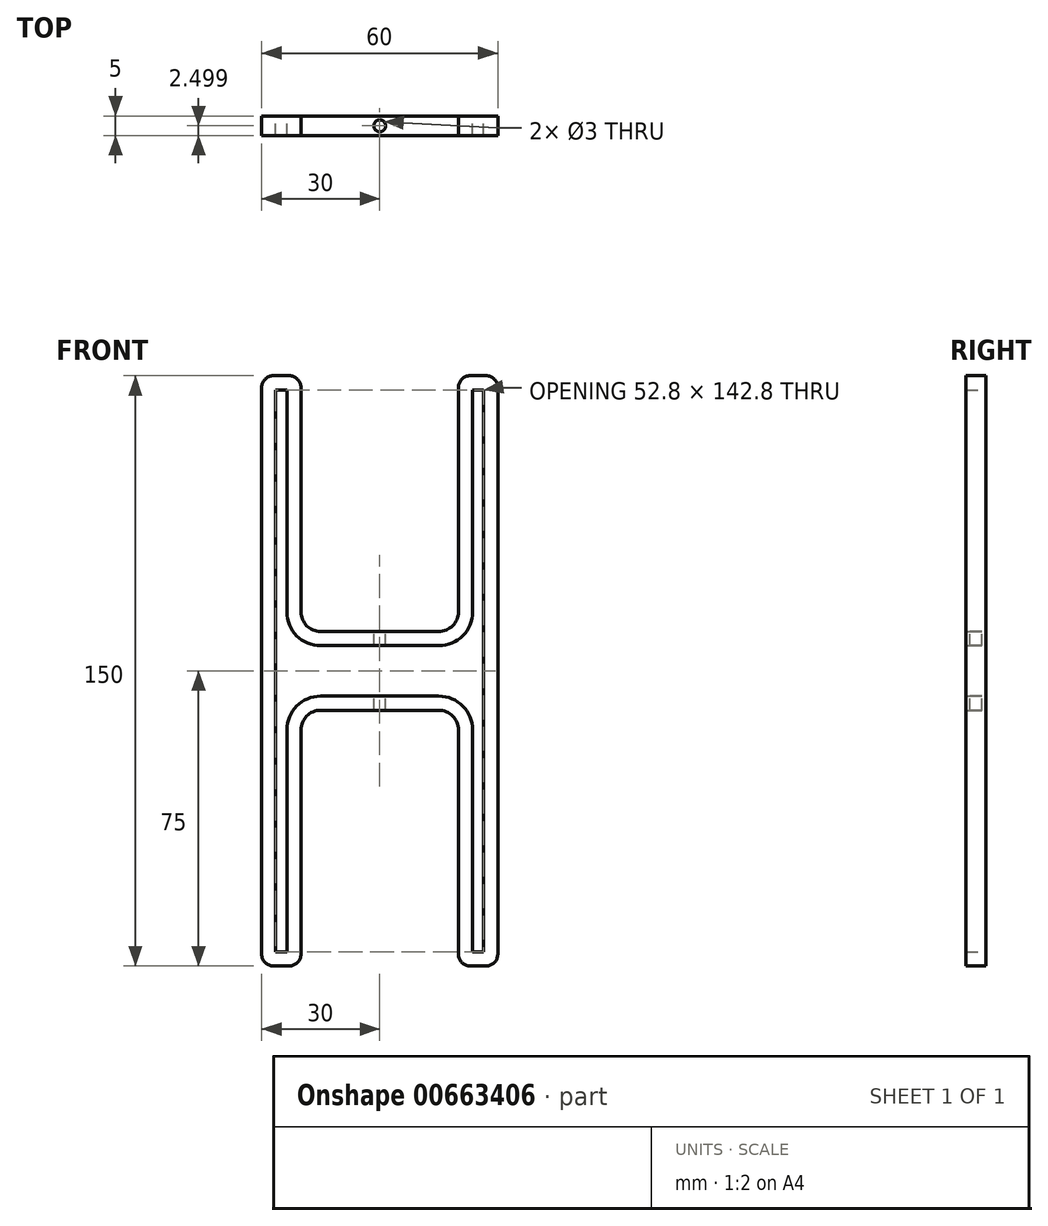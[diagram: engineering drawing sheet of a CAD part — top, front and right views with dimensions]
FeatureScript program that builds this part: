
annotation { "Feature Type Name" : "Feature", "Feature Type Description" : "" }
export const myFeature = defineFeature(function(context is Context, id is Id, definition is map)
    precondition{}
    {
        {
            var Q0;
            Q0=qCreatedBy(makeId("Front.planeOp"),FACE);
            var sketch = newSketch(context, id + "F0", { "sketchPlane" : qUnion([Q0])});
            skLineSegment(sketch, "E0.bottom", {"start": v(-27, 75) * mm, "end": v(-23, 75) * mm});
            skLineSegment(sketch, "E0.top", {"start": v(-27, -75) * mm, "end": v(-23, -75) * mm});
            skLineSegment(sketch, "E0.left", {"start": v(-30, 72) * mm, "end": v(-30, -72) * mm});
            skLineSegment(sketch, "E0.right", {"start": v(30, 72) * mm, "end": v(30, -72) * mm});
            skLineSegment(sketch, "E1.top", {"start": v(-15, 10) * mm, "end": v(15, 10) * mm});
            skLineSegment(sketch, "E1.left", {"start": v(-20, 72) * mm, "end": v(-20, 15) * mm});
            skLineSegment(sketch, "E1.right", {"start": v(20, 72) * mm, "end": v(20, 15) * mm});
            skLineSegment(sketch, "E2.top", {"start": v(-15, -10) * mm, "end": v(15, -10) * mm});
            skLineSegment(sketch, "E2.left", {"start": v(-20, -72) * mm, "end": v(-20, -15) * mm});
            skLineSegment(sketch, "E2.right", {"start": v(20, -72) * mm, "end": v(20, -15) * mm});
            skLineSegment(sketch, "E3.bottom", {"start": v(20.27, 1.5) * mm, "end": v(-20.27, 1.5) * mm});
            skLineSegment(sketch, "E3.top", {"start": v(20.27, -1.5) * mm, "end": v(-20.27, -1.5) * mm});
            skLineSegment(sketch, "E3.left", {"start": v(20.27, 1.5) * mm, "end": v(20.27, -1.5) * mm});
            skLineSegment(sketch, "E3.right", {"start": v(-20.27, 1.5) * mm, "end": v(-20.27, -1.5) * mm});
            skPoint(sketch, "E4.visualSharp", {"position": v(-30, 75) * mm});
            skArc(sketch, "E4.filletArc", {"start": v(-27, 75) * mm, "mid": v(-29.12, 74.12) * mm, "end": v(-30, 72) * mm});
            skPoint(sketch, "E5.visualSharp", {"position": v(30, 75) * mm});
            skArc(sketch, "E5.filletArc", {"start": v(30, 72) * mm, "mid": v(29.12, 74.12) * mm, "end": v(27, 75) * mm});
            skPoint(sketch, "E6.visualSharp", {"position": v(30, -75) * mm});
            skArc(sketch, "E6.filletArc", {"start": v(27, -75) * mm, "mid": v(29.12, -74.12) * mm, "end": v(30, -72) * mm});
            skPoint(sketch, "E7.visualSharp", {"position": v(-30, -75) * mm});
            skArc(sketch, "E7.filletArc", {"start": v(-30, -72) * mm, "mid": v(-29.12, -74.12) * mm, "end": v(-27, -75) * mm});
            skLineSegment(sketch, "E8.trimOffspring", {"start": v(23, 75) * mm, "end": v(27, 75) * mm});
            skLineSegment(sketch, "E9.trimOffspring", {"start": v(23, -75) * mm, "end": v(27, -75) * mm});
            skPoint(sketch, "E10.visualSharp", {"position": v(20, -10) * mm});
            skArc(sketch, "E10.filletArc", {"start": v(20, -15) * mm, "mid": v(18.54, -11.46) * mm, "end": v(15, -10) * mm});
            skPoint(sketch, "E11.visualSharp", {"position": v(-20, -10) * mm});
            skArc(sketch, "E11.filletArc", {"start": v(-15, -10) * mm, "mid": v(-18.54, -11.46) * mm, "end": v(-20, -15) * mm});
            skPoint(sketch, "E12.visualSharp", {"position": v(-20, 10) * mm});
            skArc(sketch, "E12.filletArc", {"start": v(-20, 15) * mm, "mid": v(-18.54, 11.46) * mm, "end": v(-15, 10) * mm});
            skPoint(sketch, "E13.visualSharp", {"position": v(20, 10) * mm});
            skArc(sketch, "E13.filletArc", {"start": v(15, 10) * mm, "mid": v(18.54, 11.46) * mm, "end": v(20, 15) * mm});
            skPoint(sketch, "E14.visualSharp", {"position": v(-20, 75) * mm});
            skArc(sketch, "E14.filletArc", {"start": v(-20, 72) * mm, "mid": v(-20.88, 74.12) * mm, "end": v(-23, 75) * mm});
            skPoint(sketch, "E15.visualSharp", {"position": v(20, 75) * mm});
            skArc(sketch, "E15.filletArc", {"start": v(23, 75) * mm, "mid": v(20.88, 74.12) * mm, "end": v(20, 72) * mm});
            skPoint(sketch, "E16.visualSharp", {"position": v(20, -75) * mm});
            skArc(sketch, "E16.filletArc", {"start": v(20, -72) * mm, "mid": v(20.88, -74.12) * mm, "end": v(23, -75) * mm});
            skPoint(sketch, "E17.visualSharp", {"position": v(-20, -75) * mm});
            skArc(sketch, "E17.filletArc", {"start": v(-23, -75) * mm, "mid": v(-20.88, -74.12) * mm, "end": v(-20, -72) * mm});
            skLineSegment(sketch, "E18.0", {"start": v(-26.4, -71.4) * mm, "end": v(-23.6, -71.4) * mm});
            skLineSegment(sketch, "E18.1", {"start": v(-26.4, 71.4) * mm, "end": v(-26.4, -71.4) * mm});
            skLineSegment(sketch, "E18.2", {"start": v(-26.4, 71.4) * mm, "end": v(-23.6, 71.4) * mm});
            skLineSegment(sketch, "E18.3", {"start": v(-23.6, 71.4) * mm, "end": v(-23.6, 15) * mm});
            skArc(sketch, "E18.4", {"start": v(-23.6, 15) * mm, "mid": v(-21.08, 8.92) * mm, "end": v(-15, 6.4) * mm});
            skLineSegment(sketch, "E18.5", {"start": v(23.6, -71.4) * mm, "end": v(23.6, -15) * mm});
            skArc(sketch, "E18.6", {"start": v(23.6, -15) * mm, "mid": v(21.08, -8.92) * mm, "end": v(15, -6.4) * mm});
            skLineSegment(sketch, "E18.7", {"start": v(-15, -6.4) * mm, "end": v(15, -6.4) * mm});
            skArc(sketch, "E18.8", {"start": v(-15, -6.4) * mm, "mid": v(-21.08, -8.92) * mm, "end": v(-23.6, -15) * mm});
            skLineSegment(sketch, "E18.9", {"start": v(23.6, -71.4) * mm, "end": v(26.4, -71.4) * mm});
            skLineSegment(sketch, "E18.10", {"start": v(26.4, 71.4) * mm, "end": v(26.4, -71.4) * mm});
            skLineSegment(sketch, "E18.11", {"start": v(23.6, 71.4) * mm, "end": v(26.4, 71.4) * mm});
            skLineSegment(sketch, "E18.12", {"start": v(23.6, 71.4) * mm, "end": v(23.6, 15) * mm});
            skArc(sketch, "E18.13", {"start": v(15, 6.4) * mm, "mid": v(21.08, 8.92) * mm, "end": v(23.6, 15) * mm});
            skLineSegment(sketch, "E18.14", {"start": v(-23.6, -71.4) * mm, "end": v(-23.6, -15) * mm});
            skLineSegment(sketch, "E18.15", {"start": v(-15, 6.4) * mm, "end": v(15, 6.4) * mm});
            skSolve(sketch);
        }
        {
            var Q0;
            Q0=makeQuery(id+"F0.imprint","IMPRINT",FACE,{"disambiguationData":[TD([[makeQuery(id+"F0.imprint","IMPRINT",EDGE,{"derivedFrom":sQuery(id+"F0.wireOp",EDGE,"E0.bottom")}),-1.0]])]});
            extrude(context, id + "F1", {"entities" : qUnion([Q0]), "depth" : 5 * mm, "offsetDistance" : 25 * mm});
        }
        {
            var Q0;
            Q0=makeQuery(id+"F1.opExtrude","SWEPT_FACE",FACE,{"disambiguationData":[OSD([sQuery(id+"F0.wireOp",EDGE,"E1.top")])]});
            var sketch = newSketch(context, id + "F2", { "sketchPlane" : qUnion([Q0])});
            skCircle(sketch, "E19", {"center": v(0, -2.5) * mm, "radius": 1.5 * mm});
            skSolve(sketch);
        }
        {
            var Q0;
            Q0 = qSketchRegion(id + "F2", true);
            extrude(context, id + "F3", {"entities" : qUnion([Q0]), "operationType" : NewBodyOperationType.REMOVE, "oppositeDirection" : true, "depth" : 25 * mm, "offsetDistance" : 25 * mm});
        }
    });
